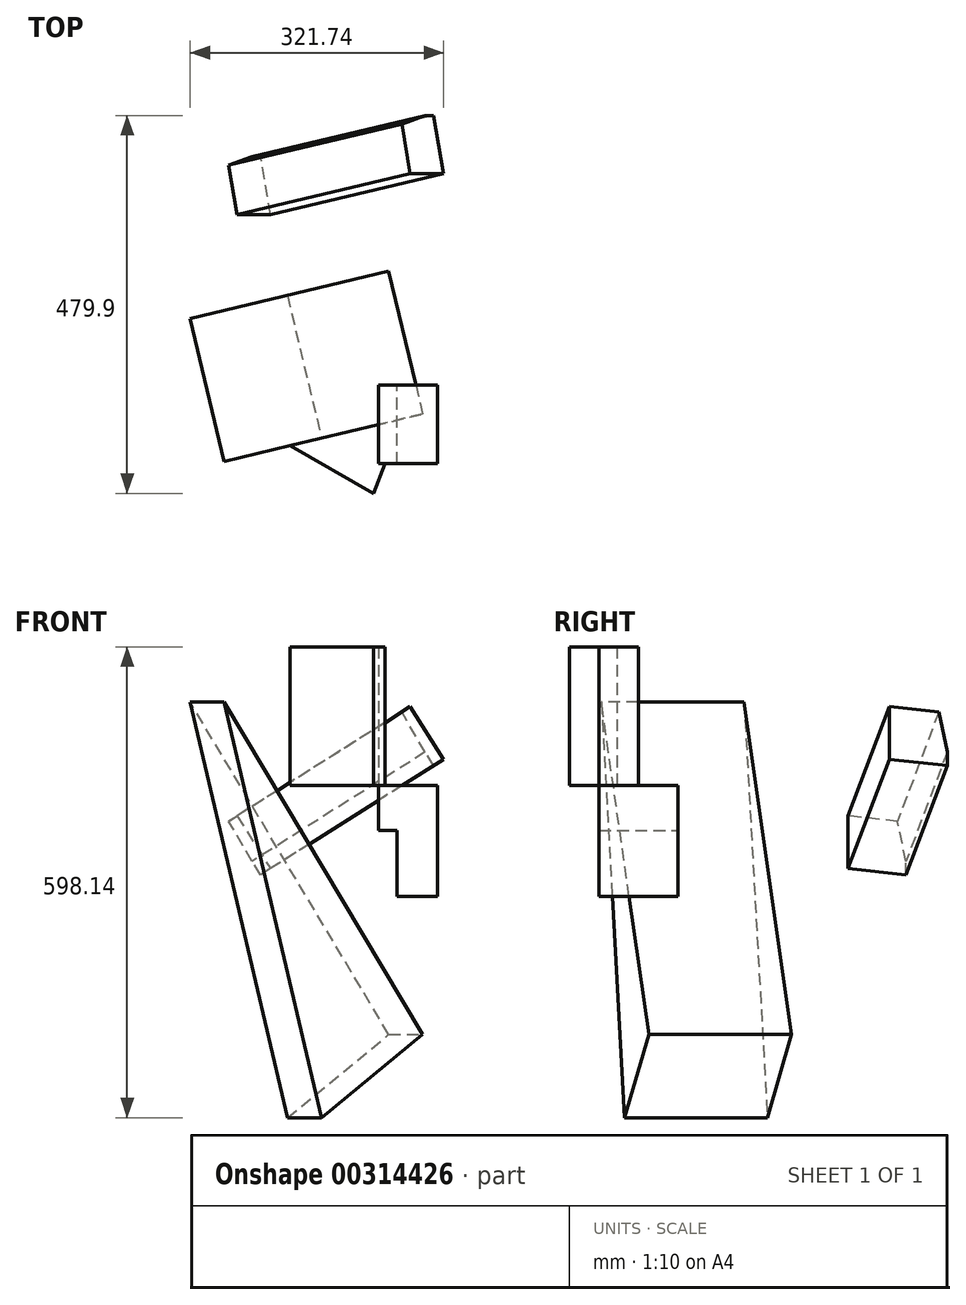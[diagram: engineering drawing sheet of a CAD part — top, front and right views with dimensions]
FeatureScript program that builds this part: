
annotation { "Feature Type Name" : "Feature", "Feature Type Description" : "" }
export const myFeature = defineFeature(function(context is Context, id is Id, definition is map)
    precondition{}
    {
        {
            var Q0;
            Q0=qCreatedBy(makeId("Front.planeOp"),FACE);
            var sketch = newSketch(context, id + "F0", { "sketchPlane" : qUnion([Q0])});
            skLineSegment(sketch, "E0", {"start": v(0, 57.09) * mm, "end": v(75, 57.09) * mm});
            skLineSegment(sketch, "E1", {"start": v(75, 57.09) * mm, "end": v(75, -83.4) * mm});
            skLineSegment(sketch, "E2", {"start": v(75, -83.4) * mm, "end": v(23.5, -83.4) * mm});
            skLineSegment(sketch, "E3", {"start": v(23.5, -83.4) * mm, "end": v(23.5, 0) * mm});
            skLineSegment(sketch, "E4", {"start": v(23.5, 0) * mm, "end": v(0, 0) * mm});
            skLineSegment(sketch, "E5", {"start": v(0, 0) * mm, "end": v(0, 57.09) * mm});
            skSolve(sketch);
        }
        {
            var Q0;
            Q0=makeQuery(id+"F0.imprint","IMPRINT",FACE,{"disambiguationData":[TD([[makeQuery(id+"F0.imprint","IMPRINT",EDGE,{"derivedFrom":sQuery(id+"F0.wireOp",EDGE,"E0")}),-1.0]])]});
            extrude(context, id + "F1", {"entities" : qUnion([Q0]), "depth" : 100 * mm});
        }
        {
            var Q0;
            Q0=makeQuery(id+"F1.opExtrude","SWEPT_FACE",FACE,{"disambiguationData":[OSD([sQuery(id+"F0.wireOp",EDGE,"E0")])]});
            var sketch = newSketch(context, id + "F2", { "sketchPlane" : qUnion([Q0])});
            skLineSegment(sketch, "E6", {"start": v(-6.44, -137.69) * mm, "end": v(29.33, -43.28) * mm});
            skLineSegment(sketch, "E7", {"start": v(29.33, -43.28) * mm, "end": v(-112.59, -77.14) * mm});
            skLineSegment(sketch, "E8", {"start": v(-112.59, -77.14) * mm, "end": v(-6.44, -137.69) * mm});
            skSolve(sketch);
        }
        {
            var Q0;
            {var subQ0=sQuery(id+"F2.wireOp",EDGE,"E8");Q0=makeQuery(id+"F2.imprint","IMPRINT",FACE,{"disambiguationData":[TD([[makeQuery(id+"F2.imprint","IMPRINT",EDGE,{"derivedFrom":subQ0}),1.0]])]});}
            extrude(context, id + "F3", {"entities" : qUnion([Q0]), "depth" : 176.32 * mm});
        }
        {
            var Q0;
            Q0=makeQuery(id+"F3.opExtrude","SWEPT_FACE",FACE,{"disambiguationData":[OSD([sQuery(id+"F2.wireOp",EDGE,"E7")])]});
            var sketch = newSketch(context, id + "F4", { "sketchPlane" : qUnion([Q0])});
            skLineSegment(sketch, "E9", {"start": v(213.33, 163.1) * mm, "end": v(86.42, -364.73) * mm});
            skLineSegment(sketch, "E10", {"start": v(86.42, -364.73) * mm, "end": v(-45.89, -258.91) * mm});
            skLineSegment(sketch, "E11", {"start": v(-45.89, -258.91) * mm, "end": v(213.33, 163.1) * mm});
            skSolve(sketch);
        }
        {
            var Q0;
            Q0=makeQuery(id+"F4.imprint","IMPRINT",FACE,{"disambiguationData":[TD([[makeQuery(id+"F4.imprint","IMPRINT",EDGE,{"derivedFrom":sQuery(id+"F4.wireOp",EDGE,"E9")}),-1.0]])]});
            extrude(context, id + "F5", {"entities" : qUnion([Q0]), "depth" : 186.3 * mm});
        }
        {
            var Q0;
            Q0=makeQuery(id+"F5.opExtrude","SWEPT_FACE",FACE,{"disambiguationData":[OSD([sQuery(id+"F4.wireOp",EDGE,"E11")])]});
            var sketch = newSketch(context, id + "F6", { "sketchPlane" : qUnion([Q0])});
            skLineSegment(sketch, "E12", {"start": v(240.07, 141.35) * mm, "end": v(240.07, 32.52) * mm});
            skLineSegment(sketch, "E13", {"start": v(240.07, 32.52) * mm, "end": v(315.07, 32.52) * mm});
            skLineSegment(sketch, "E14", {"start": v(315.07, 32.52) * mm, "end": v(315.07, 52.76) * mm});
            skLineSegment(sketch, "E15", {"start": v(315.07, 52.76) * mm, "end": v(304.18, 111.63) * mm});
            skLineSegment(sketch, "E16", {"start": v(304.18, 111.63) * mm, "end": v(240.07, 111.63) * mm});
            skLineSegment(sketch, "E17", {"start": v(240.07, 111.63) * mm, "end": v(240.07, 141.35) * mm});
            skSolve(sketch);
        }
        {
            var Q0;
            Q0 = qSketchRegion(id + "F6", true);
            extrude(context, id + "F7", {"entities" : qUnion([Q0]), "depth" : 265.14 * mm});
        }
    });
